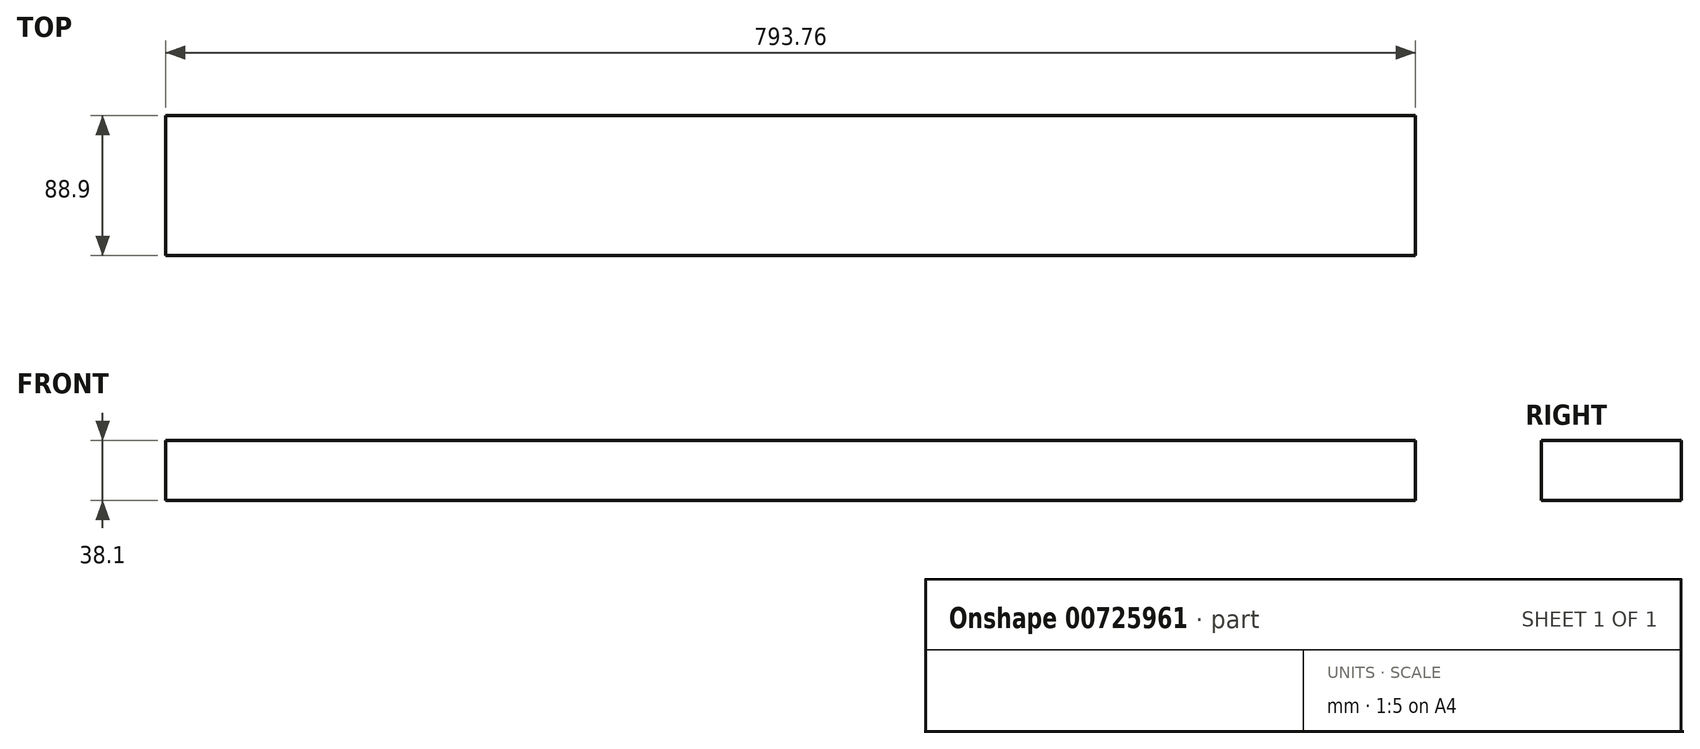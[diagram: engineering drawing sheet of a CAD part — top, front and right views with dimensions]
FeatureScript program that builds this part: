
annotation { "Feature Type Name" : "Feature", "Feature Type Description" : "" }
export const myFeature = defineFeature(function(context is Context, id is Id, definition is map)
    precondition{}
    {
        {
            var Q0;
            Q0=qCreatedBy(makeId("Top.planeOp"),FACE);
            var sketch = newSketch(context, id + "F0", { "sketchPlane" : qUnion([Q0])});
            skLineSegment(sketch, "E0.bottom", {"start": v(396.88, -44.45) * mm, "end": v(-396.88, -44.45) * mm});
            skLineSegment(sketch, "E0.top", {"start": v(396.88, 44.45) * mm, "end": v(-396.88, 44.45) * mm});
            skLineSegment(sketch, "E0.left", {"start": v(396.88, -44.45) * mm, "end": v(396.88, 44.45) * mm});
            skLineSegment(sketch, "E0.right", {"start": v(-396.88, -44.45) * mm, "end": v(-396.88, 44.45) * mm});
            skPoint(sketch, "E0.middle", {"position": v(0, 0) * mm});
            skSolve(sketch);
        }
        {
            var Q0;
            Q0 = qSketchRegion(id + "F0", true);
            extrude(context, id + "F1", {"entities" : qUnion([Q0]), "depth" : 38.1 * mm, "offsetDistance" : 25.4 * mm});
        }
    });
